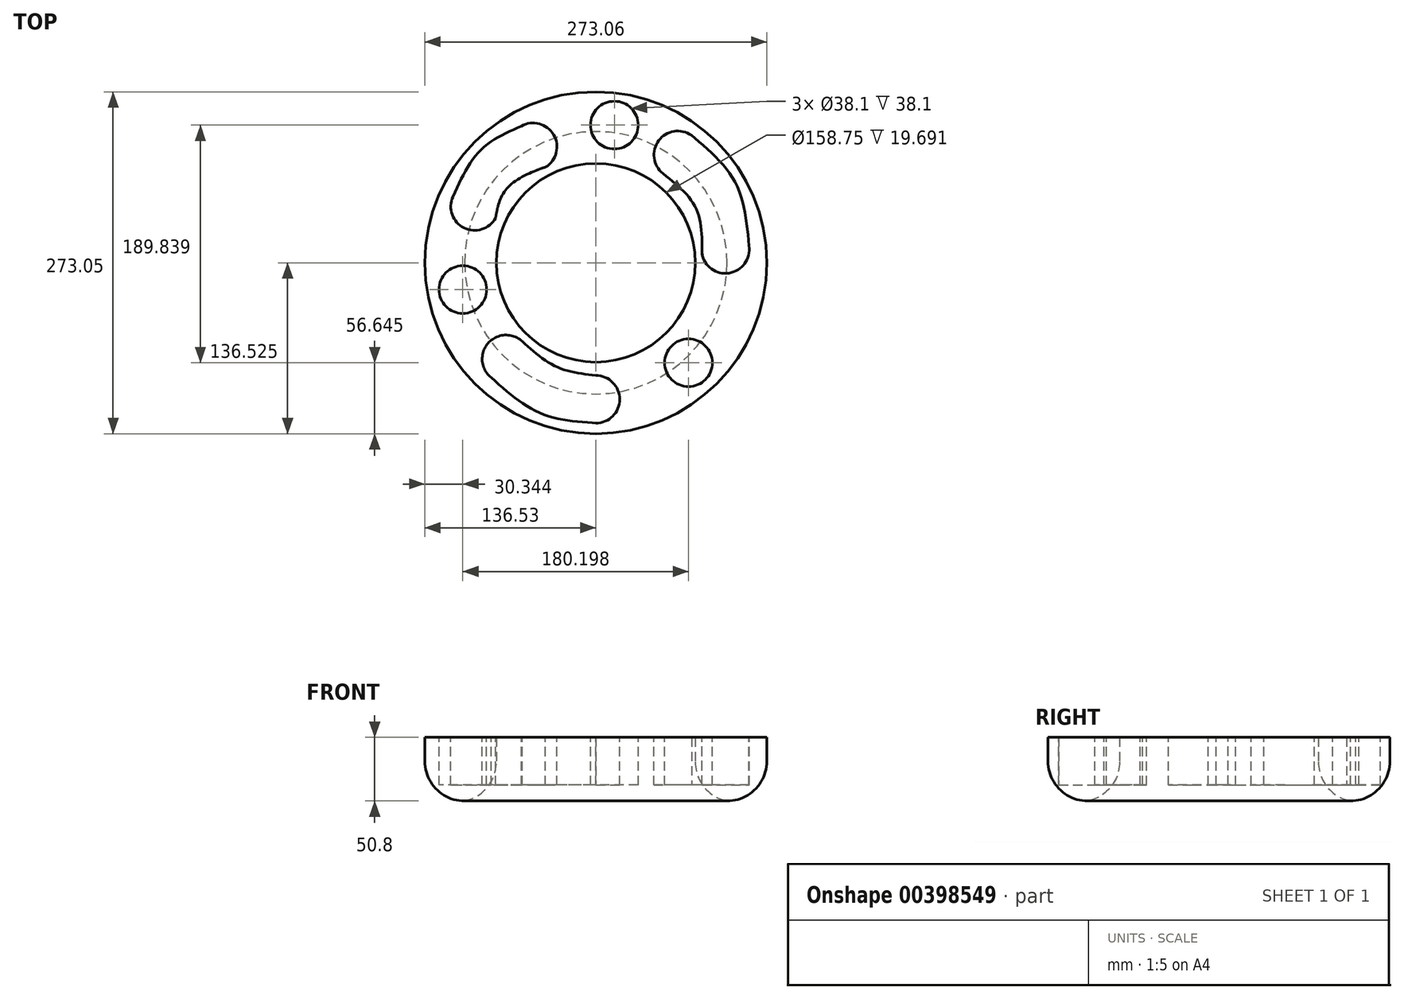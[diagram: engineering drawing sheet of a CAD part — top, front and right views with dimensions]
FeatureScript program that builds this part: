
annotation { "Feature Type Name" : "Feature", "Feature Type Description" : "" }
export const myFeature = defineFeature(function(context is Context, id is Id, definition is map)
    precondition{}
    {
        {
            var Q0;
            Q0=qCreatedBy(makeId("Top.planeOp"),FACE);
            var sketch = newSketch(context, id + "F0", { "sketchPlane" : qUnion([Q0])});
            skCircle(sketch, "E0", {"center": v(0, 2.03) * mm, "radius": 79.38 * mm});
            skCircle(sketch, "E1", {"center": v(0, 2.03) * mm, "radius": 136.53 * mm});
            skSolve(sketch);
        }
        {
            var Q0;
            Q0 = qSketchRegion(id + "F0", true);
            extrude(context, id + "F1", {"entities" : qUnion([Q0]), "depth" : 50.8 * mm});
        }
        {
            var Q0;
            Q0=makeQuery(id+"F1.opExtrude","CAP_EDGE",EDGE,{"disambiguationData":[OSD([sQuery(id+"F0.wireOp",EDGE,"E1")])],"isStart":true});
            fillet(context, id + "F2", {"entities" : qUnion([Q0]), "radius" : 31.75 * mm, "tangentPropagation" : true, "allowEdgeOverflow" : false});
        }
        {
            var Q0;
            Q0=makeQuery(id+"F1.opExtrude","CAP_EDGE",EDGE,{"disambiguationData":[OSD([sQuery(id+"F0.wireOp",EDGE,"E0")])],"isStart":true});
            fillet(context, id + "F3", {"entities" : qUnion([Q0]), "radius" : 31.75 * mm, "tangentPropagation" : true, "allowEdgeOverflow" : false});
        }
        {
            var Q0;
            Q0=makeQuery(id+"F1.opExtrude","CAP_FACE",FACE,{"disambiguationData":[OSD([sQuery(id+"F0.wireOp",EDGE,"E0"),sQuery(id+"F0.wireOp",EDGE,"E1")])],"isStart":false});
            var sketch = newSketch(context, id + "F4", { "sketchPlane" : qUnion([Q0])});
            skCircle(sketch, "E2", {"center": v(-71.68, -74.74) * mm, "radius": 19.05 * mm});
            skCircle(sketch, "E3", {"center": v(0, -107.04) * mm, "radius": 19.05 * mm});
            skCircle(sketch, "E4", {"center": v(74.01, -77.84) * mm, "radius": 19.05 * mm});
            skCircle(sketch, "E5", {"center": v(65.45, 88.22) * mm, "radius": 19.05 * mm});
            skCircle(sketch, "E6", {"center": v(103.49, 12.6) * mm, "radius": 19.05 * mm});
            skFitSpline(sketch, "E7", {"points": [v(0, -126.09) * mm, v(-44.6, -117.92) * mm, v(-83.54, -89.64) * mm], "startDerivative": vector(-93.94, 6.94) * mm, "endDerivative": vector(-73.28, 65.61) * mm});
            skFitSpline(sketch, "E8", {"points": [v(0, -87.99) * mm, v(-31.43, -80.98) * mm, v(-58.75, -60.75) * mm], "startDerivative": vector(-66.13, 7.86) * mm, "endDerivative": vector(-51.45, 46.42) * mm});
            skCircle(sketch, "E9", {"center": v(-106.19, -19.35) * mm, "radius": 19.05 * mm});
            skCircle(sketch, "E10", {"center": v(14.82, 112) * mm, "radius": 19.05 * mm});
            skCircle(sketch, "E11", {"center": v(-96.72, 46.95) * mm, "radius": 19.05 * mm});
            skCircle(sketch, "E12", {"center": v(-50.1, 94.6) * mm, "radius": 19.05 * mm});
            skFitSpline(sketch, "E13", {"points": [v(-80.02, 37.78) * mm, v(-67.17, 65.13) * mm, v(-40.14, 78.36) * mm, v(-40.72, 78.02) * mm], "startDerivative": vector(10.84, 63.14) * mm, "endDerivative": vector(-13.69, -6.92) * mm});
            skFitSpline(sketch, "E14", {"points": [v(-114.1, 54.73) * mm, v(-91.81, 92.16) * mm, v(-59.49, 111.18) * mm], "startDerivative": vector(36.74, 80.6) * mm, "endDerivative": vector(72.98, 31.66) * mm});
            skFitSpline(sketch, "E15", {"points": [v(84.7, 9.47) * mm, v(79.94, 45.68) * mm, v(53.69, 73.23) * mm], "startDerivative": vector(0.86, 77.8) * mm, "endDerivative": vector(-62.65, 49.86) * mm});
            skFitSpline(sketch, "E16", {"points": [v(122.32, 15.43) * mm, v(111.34, 66.19) * mm, v(76.4, 103.8) * mm], "startDerivative": vector(-9.79, 107.7) * mm, "endDerivative": vector(-82.1, 69.03) * mm});
            skSolve(sketch);
        }
        {
            var Q0;
            Q0=makeQuery(id+"F4.imprint","IMPRINT",FACE,{"disambiguationData":[TD([[makeQuery(id+"F4.imprint","IMPRINT",EDGE,{"derivedFrom":sQuery(id+"F4.wireOp",EDGE,"E9")}),1.0]])]});
            var Q1;
            {var subQ0=sQuery(id+"F4.wireOp",EDGE,"E2");var subQ1=makeQuery(id+"F4.imprint","INTERSECT",VERTEX,{"derivedFrom":[subQ0,sQuery(id+"F4.wireOp",EDGE,"E7")]});Q1=makeQuery(id+"F4.imprint","IMPRINT",FACE,{"disambiguationData":[TD([[makeQuery(id+"F4.imprint","IMPRINT",EDGE,{"disambiguationData":[TD([[subQ1,1.0]])],"derivedFrom":subQ0}),1.0]])]});}
            var Q2;
            {var subQ0=sQuery(id+"F4.wireOp",EDGE,"E3");var subQ1=makeQuery(id+"F4.imprint","INTERSECT",VERTEX,{"derivedFrom":[subQ0,sQuery(id+"F4.wireOp",EDGE,"E8")]});Q2=makeQuery(id+"F4.imprint","IMPRINT",FACE,{"disambiguationData":[TD([[makeQuery(id+"F4.imprint","IMPRINT",EDGE,{"disambiguationData":[TD([[subQ1,-1.0]])],"derivedFrom":subQ0}),1.0]])]});}
            var Q3;
            {var subQ3=sQuery(id+"F4.wireOp",EDGE,"E8");Q3=makeQuery(id+"F4.imprint","IMPRINT",FACE,{"disambiguationData":[TD([[makeQuery(id+"F4.imprint","IMPRINT",EDGE,{"derivedFrom":subQ3}),1.0]])]});}
            var Q4;
            Q4=makeQuery(id+"F4.imprint","IMPRINT",FACE,{"disambiguationData":[TD([[makeQuery(id+"F4.imprint","IMPRINT",EDGE,{"derivedFrom":sQuery(id+"F4.wireOp",EDGE,"E4")}),1.0]])]});
            var Q5;
            {var subQ0=sQuery(id+"F4.wireOp",EDGE,"E15");var subQ1=sQuery(id+"F4.wireOp",EDGE,"E5");var subQ2=makeQuery(id+"F4.imprint","INTERSECT",VERTEX,{"derivedFrom":[subQ1,subQ0]});Q5=makeQuery(id+"F4.imprint","IMPRINT",FACE,{"disambiguationData":[TD([[makeQuery(id+"F4.imprint","IMPRINT",EDGE,{"disambiguationData":[TD([[subQ2,-1.0]])],"derivedFrom":subQ1}),-1.0]])]});}
            var Q6;
            {var subQ0=sQuery(id+"F4.wireOp",EDGE,"E6");var subQ1=makeQuery(id+"F4.imprint","INTERSECT",VERTEX,{"derivedFrom":[subQ0,sQuery(id+"F4.wireOp",EDGE,"E16")]});Q6=makeQuery(id+"F4.imprint","IMPRINT",FACE,{"disambiguationData":[TD([[makeQuery(id+"F4.imprint","IMPRINT",EDGE,{"disambiguationData":[TD([[subQ1,-1.0]])],"derivedFrom":subQ0}),1.0]])]});}
            var Q7;
            {var subQ0=sQuery(id+"F4.wireOp",EDGE,"E5");var subQ1=makeQuery(id+"F4.imprint","INTERSECT",VERTEX,{"derivedFrom":[subQ0,sQuery(id+"F4.wireOp",EDGE,"E15")]});Q7=makeQuery(id+"F4.imprint","IMPRINT",FACE,{"disambiguationData":[TD([[makeQuery(id+"F4.imprint","IMPRINT",EDGE,{"disambiguationData":[TD([[subQ1,1.0]])],"derivedFrom":subQ0}),1.0]])]});}
            var Q8;
            {var subQ0=sQuery(id+"F4.wireOp",EDGE,"E14");var subQ1=sQuery(id+"F4.wireOp",EDGE,"E11");var subQ2=makeQuery(id+"F4.imprint","INTERSECT",VERTEX,{"disambiguationData":[OD(1.0)],"derivedFrom":[subQ1,subQ0]});Q8=makeQuery(id+"F4.imprint","IMPRINT",FACE,{"disambiguationData":[TD([[makeQuery(id+"F4.imprint","IMPRINT",EDGE,{"disambiguationData":[TD([[subQ2,1.0]])],"derivedFrom":subQ1}),1.0]])]});}
            var Q9;
            {var subQ0=sQuery(id+"F4.wireOp",EDGE,"E14");var subQ1=sQuery(id+"F4.wireOp",EDGE,"E11");var subQ2=makeQuery(id+"F4.imprint","INTERSECT",VERTEX,{"disambiguationData":[OD(1.0)],"derivedFrom":[subQ1,subQ0]});Q9=makeQuery(id+"F4.imprint","IMPRINT",FACE,{"disambiguationData":[TD([[makeQuery(id+"F4.imprint","IMPRINT",EDGE,{"disambiguationData":[TD([[subQ2,1.0]])],"derivedFrom":subQ1}),-1.0]])]});}
            var Q10;
            {var subQ0=sQuery(id+"F4.wireOp",EDGE,"E12");var subQ1=makeQuery(id+"F4.imprint","INTERSECT",VERTEX,{"derivedFrom":[subQ0,sQuery(id+"F4.wireOp",EDGE,"E14")]});Q10=makeQuery(id+"F4.imprint","IMPRINT",FACE,{"disambiguationData":[TD([[makeQuery(id+"F4.imprint","IMPRINT",EDGE,{"disambiguationData":[TD([[subQ1,-1.0]])],"derivedFrom":subQ0}),1.0]])]});}
            var Q11;
            Q11=makeQuery(id+"F4.imprint","IMPRINT",FACE,{"disambiguationData":[TD([[makeQuery(id+"F4.imprint","IMPRINT",EDGE,{"derivedFrom":sQuery(id+"F4.wireOp",EDGE,"E10")}),1.0]])]});
            extrude(context, id + "F5", {"entities" : qUnion([Q0, Q1, Q2, Q3, Q4, Q5, Q6, Q7, Q8, Q9, Q10, Q11]), "operationType" : NewBodyOperationType.REMOVE, "oppositeDirection" : true, "depth" : 38.1 * mm});
        }
    });
